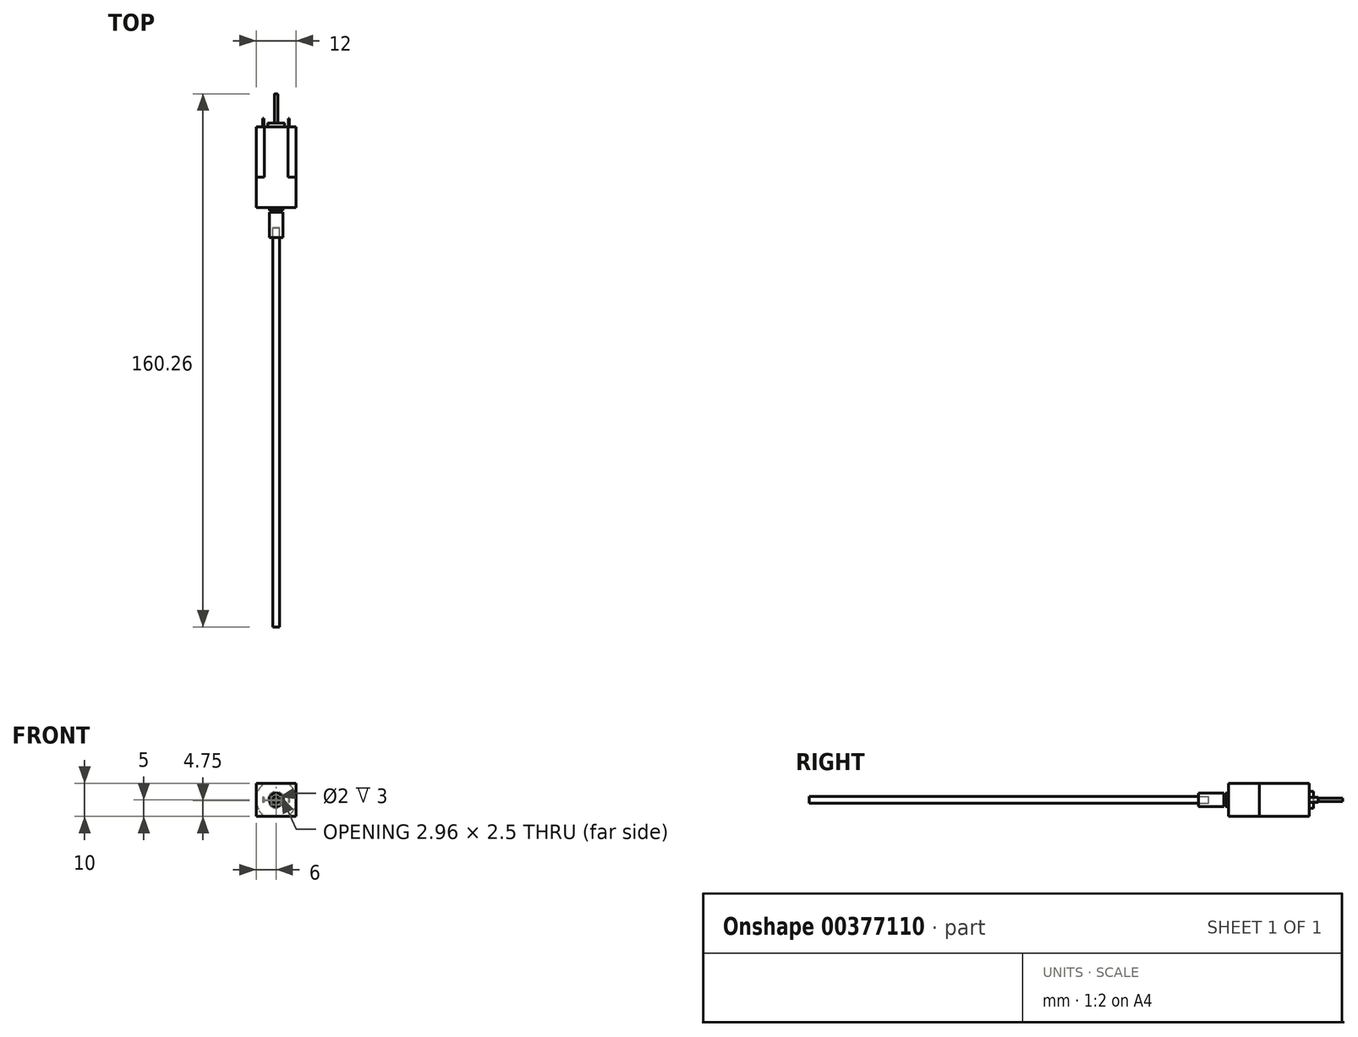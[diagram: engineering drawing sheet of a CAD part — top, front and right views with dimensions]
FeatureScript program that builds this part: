
annotation { "Feature Type Name" : "Feature", "Feature Type Description" : "" }
export const myFeature = defineFeature(function(context is Context, id is Id, definition is map)
    precondition{}
    {
        {
            var Q0;
            Q0=qCreatedBy(makeId("Right.planeOp"),FACE);
            var sketch = newSketch(context, id + "F0", { "sketchPlane" : qUnion([Q0])});
            skLineSegment(sketch, "E0.bottom", {"start": v(12.12, 5) * mm, "end": v(-12.13, 5) * mm});
            skLineSegment(sketch, "E0.top", {"start": v(12.13, -5) * mm, "end": v(-12.12, -5) * mm});
            skLineSegment(sketch, "E0.left", {"start": v(12.12, 5) * mm, "end": v(12.13, -5) * mm});
            skLineSegment(sketch, "E0.right", {"start": v(-12.13, 5) * mm, "end": v(-12.12, -5) * mm});
            skPoint(sketch, "E0.middle", {"position": v(0, 0) * mm});
            skSolve(sketch);
        }
        {
            var Q0;
            Q0 = qSketchRegion(id + "F0", true);
            extrude(context, id + "F1", {"entities" : qUnion([Q0]), "endBound" : BoundingType.SYMMETRIC, "depth" : 12 * mm});
        }
        {
            var Q0;
            Q0=makeQuery(id+"F1.opExtrude","SWEPT_FACE",FACE,{"disambiguationData":[OSD([sQuery(id+"F0.wireOp",EDGE,"E0.left")])]});
            var sketch = newSketch(context, id + "F2", { "sketchPlane" : qUnion([Q0])});
            skArc(sketch, "E1", {"start": v(-3.6, 5) * mm, "mid": v(-6, 0) * mm, "end": v(-3.6, -5) * mm});
            skLineSegment(sketch, "E2", {"start": v(-3.6, 5) * mm, "end": v(-6, 5) * mm});
            skLineSegment(sketch, "E3", {"start": v(-6, 5) * mm, "end": v(-6, -5) * mm});
            skLineSegment(sketch, "E4", {"start": v(-6, -5) * mm, "end": v(-3.6, -5) * mm});
            skLineSegment(sketch, "E5.MirrorCS", {"start": v(6, -5) * mm, "end": v(3.6, -5) * mm});
            skLineSegment(sketch, "E6.MirrorCS", {"start": v(3.6, 5) * mm, "end": v(6, 5) * mm});
            skArc(sketch, "E7.MirrorCS", {"start": v(3.6, 5) * mm, "mid": v(6, 0) * mm, "end": v(3.6, -5) * mm});
            skLineSegment(sketch, "E8.MirrorCS", {"start": v(6, 5) * mm, "end": v(6, -5) * mm});
            skSolve(sketch);
        }
        {
            var Q0;
            Q0 = qSketchRegion(id + "F2", true);
            extrude(context, id + "F3", {"entities" : qUnion([Q0]), "operationType" : NewBodyOperationType.REMOVE, "oppositeDirection" : true, "depth" : 15 * mm});
        }
        {
            var Q0;
            Q0=makeQuery(id+"F1.opExtrude","SWEPT_FACE",FACE,{"disambiguationData":[OSD([sQuery(id+"F0.wireOp",EDGE,"E0.right")])]});
            var sketch = newSketch(context, id + "F4", { "sketchPlane" : qUnion([Q0])});
            skCircle(sketch, "E9", {"center": v(0, 0) * mm, "radius": 2.02 * mm});
            skSolve(sketch);
        }
        {
            var Q0;
            Q0 = qSketchRegion(id + "F4", true);
            extrude(context, id + "F5", {"entities" : qUnion([Q0]), "operationType" : NewBodyOperationType.ADD, "depth" : 4.5 * mm});
        }
        {
            var Q0;
            Q0=makeQuery(id+"F5.opExtrude","CAP_FACE",FACE,{"disambiguationData":[OSD([sQuery(id+"F4.wireOp",EDGE,"E9")])],"isStart":false});
            var sketch = newSketch(context, id + "F6", { "sketchPlane" : qUnion([Q0])});
            skCircle(sketch, "E10", {"center": v(0, 0) * mm, "radius": 1.5 * mm});
            skCircle(sketch, "E11.0", {"center": v(0, 0) * mm, "radius": 2.02 * mm});
            skSolve(sketch);
        }
        {
            var Q0;
            Q0 = qSketchRegion(id + "F6", true);
            extrude(context, id + "F7", {"entities" : qUnion([Q0]), "operationType" : NewBodyOperationType.REMOVE, "oppositeDirection" : true, "depth" : 3.6 * mm});
        }
        {
            var Q0;
            Q0=makeQuery(id+"F5.opExtrude","CAP_FACE",FACE,{"disambiguationData":[OSD([sQuery(id+"F4.wireOp",EDGE,"E9")])],"isStart":false});
            var sketch = newSketch(context, id + "F8", { "sketchPlane" : qUnion([Q0])});
            skLineSegment(sketch, "E12", {"start": v(-1.12, 1) * mm, "end": v(1.12, 1) * mm});
            skArc(sketch, "E13.0", {"start": v(1.12, 1) * mm, "mid": v(0, 1.5) * mm, "end": v(-1.12, 1) * mm});
            skSolve(sketch);
        }
        {
            var Q0;
            Q0 = qSketchRegion(id + "F8", true);
            var Q1;
            Q1=makeQuery(id+"F7.boolean.opBoolean","COPY",FACE,{"derivedFrom":makeQuery(id+"F7.opExtrude","CAP_FACE",FACE,{"disambiguationData":[OSD([sQuery(id+"F6.wireOp",EDGE,"E10"),sQuery(id+"F6.wireOp",EDGE,"E11.0")])],"isStart":false})});
            extrude(context, id + "F9", {"entities" : qUnion([Q0]), "operationType" : NewBodyOperationType.REMOVE, "endBound" : BoundingType.UP_TO_SURFACE, "oppositeDirection" : true, "endBoundEntityFace" : qUnion([Q1]), "depth" : 25 * mm});
        }
        {
            var Q0;
            Q0=makeQuery(id+"F1.opExtrude","SWEPT_FACE",FACE,{"disambiguationData":[OSD([sQuery(id+"F0.wireOp",EDGE,"E0.left")])]});
            var sketch = newSketch(context, id + "F10", { "sketchPlane" : qUnion([Q0])});
            skCircle(sketch, "E14", {"center": v(0, 0) * mm, "radius": 2.5 * mm});
            skSolve(sketch);
        }
        {
            var Q0;
            Q0 = qSketchRegion(id + "F10", true);
            extrude(context, id + "F11", {"entities" : qUnion([Q0]), "operationType" : NewBodyOperationType.ADD, "depth" : 1.2 * mm});
        }
        {
            var Q0;
            Q0=makeQuery(id+"F1.opExtrude","SWEPT_FACE",FACE,{"disambiguationData":[OSD([sQuery(id+"F0.wireOp",EDGE,"E0.left")])]});
            var sketch = newSketch(context, id + "F12", { "sketchPlane" : qUnion([Q0])});
            skLineSegment(sketch, "E15.bottom", {"start": v(-3.65, 0.75) * mm, "end": v(-4, 0.75) * mm});
            skLineSegment(sketch, "E15.top", {"start": v(-3.65, -0.75) * mm, "end": v(-4, -0.75) * mm});
            skLineSegment(sketch, "E15.left", {"start": v(-3.65, 0.75) * mm, "end": v(-3.65, -0.75) * mm});
            skLineSegment(sketch, "E15.right", {"start": v(-4, 0.75) * mm, "end": v(-4, -0.75) * mm});
            skPoint(sketch, "E15.middle", {"position": v(-3.83, 0) * mm});
            skLineSegment(sketch, "E16.MirrorCS", {"start": v(3.65, 0.75) * mm, "end": v(4, 0.75) * mm});
            skLineSegment(sketch, "E17.MirrorCS", {"start": v(3.65, -0.75) * mm, "end": v(4, -0.75) * mm});
            skPoint(sketch, "E18.MirrorP", {"position": v(3.83, 0) * mm});
            skLineSegment(sketch, "E19.MirrorCS", {"start": v(4, 0.75) * mm, "end": v(4, -0.75) * mm});
            skLineSegment(sketch, "E20.MirrorCS", {"start": v(3.65, 0.75) * mm, "end": v(3.65, -0.75) * mm});
            skSolve(sketch);
        }
        {
            var Q0;
            Q0 = qSketchRegion(id + "F12", true);
            extrude(context, id + "F13", {"entities" : qUnion([Q0]), "operationType" : NewBodyOperationType.ADD, "depth" : 2.6 * mm});
        }
        {
            var Q0;
            Q0=makeQuery(id+"F11.opExtrude","CAP_FACE",FACE,{"disambiguationData":[OSD([sQuery(id+"F10.wireOp",EDGE,"E14")])],"isStart":false});
            var sketch = newSketch(context, id + "F14", { "sketchPlane" : qUnion([Q0])});
            skCircle(sketch, "E21", {"center": v(0, 0) * mm, "radius": 0.5 * mm});
            skSolve(sketch);
        }
        {
            var Q0;
            Q0 = qSketchRegion(id + "F14", true);
            extrude(context, id + "F15", {"entities" : qUnion([Q0]), "operationType" : NewBodyOperationType.ADD, "depth" : 8.8 * mm});
        }
        {
            var Q0;
            Q0=makeQuery(id+"F5.opExtrude","CAP_FACE",FACE,{"disambiguationData":[OSD([sQuery(id+"F4.wireOp",EDGE,"E9")])],"isStart":false});
            var sketch = newSketch(context, id + "F16", { "sketchPlane" : qUnion([Q0])});
            skCircle(sketch, "E22.0.0", {"center": v(0, 0) * mm, "radius": 2.02 * mm});
            skLineSegment(sketch, "E23.0", {"start": v(-1.12, 1) * mm, "end": v(1.12, 1) * mm});
            skArc(sketch, "E24.0", {"start": v(-1.12, 1) * mm, "mid": v(0, -1.5) * mm, "end": v(1.12, 1) * mm});
            skSolve(sketch);
        }
        {
            var Q0;
            Q0 = qSketchRegion(id + "F16", true);
            extrude(context, id + "F17", {"entities" : qUnion([Q0]), "oppositeDirection" : true, "depth" : 3.1 * mm});
        }
        {
            var Q0;
            Q0=makeQuery(id+"F17.opExtrude","CAP_FACE",FACE,{"disambiguationData":[OSD([sQuery(id+"F16.wireOp",EDGE,"E22.0.0"),sQuery(id+"F16.wireOp",EDGE,"E23.0"),sQuery(id+"F16.wireOp",EDGE,"E24.0")])],"isStart":true});
            var sketch = newSketch(context, id + "F18", { "sketchPlane" : qUnion([Q0])});
            skCircle(sketch, "E25.0", {"center": v(0, 0) * mm, "radius": 2.02 * mm});
            skSolve(sketch);
        }
        {
            var Q0;
            Q0 = qSketchRegion(id + "F18", true);
            extrude(context, id + "F19", {"entities" : qUnion([Q0]), "operationType" : NewBodyOperationType.ADD, "depth" : 4.5 * mm});
        }
        {
            var Q0;
            Q0=makeQuery(id+"F19.opExtrude","CAP_FACE",FACE,{"disambiguationData":[OSD([sQuery(id+"F18.wireOp",EDGE,"E25.0")])],"isStart":false});
            var sketch = newSketch(context, id + "F20", { "sketchPlane" : qUnion([Q0])});
            skCircle(sketch, "E26", {"center": v(0, 0) * mm, "radius": 1 * mm});
            skSolve(sketch);
        }
        {
            var Q0;
            Q0 = qSketchRegion(id + "F20", true);
            extrude(context, id + "F21", {"entities" : qUnion([Q0]), "operationType" : NewBodyOperationType.REMOVE, "oppositeDirection" : true, "depth" : 3 * mm});
        }
        {
            var Q0;
            Q0=makeQuery(id+"F21.boolean.opBoolean","COPY",FACE,{"derivedFrom":makeQuery(id+"F21.opExtrude","CAP_FACE",FACE,{"disambiguationData":[OSD([sQuery(id+"F20.wireOp",EDGE,"E26")])],"isStart":false})});
            extrude(context, id + "F22", {"entities" : qUnion([Q0]), "depth" : 120 * mm});
        }
    });
